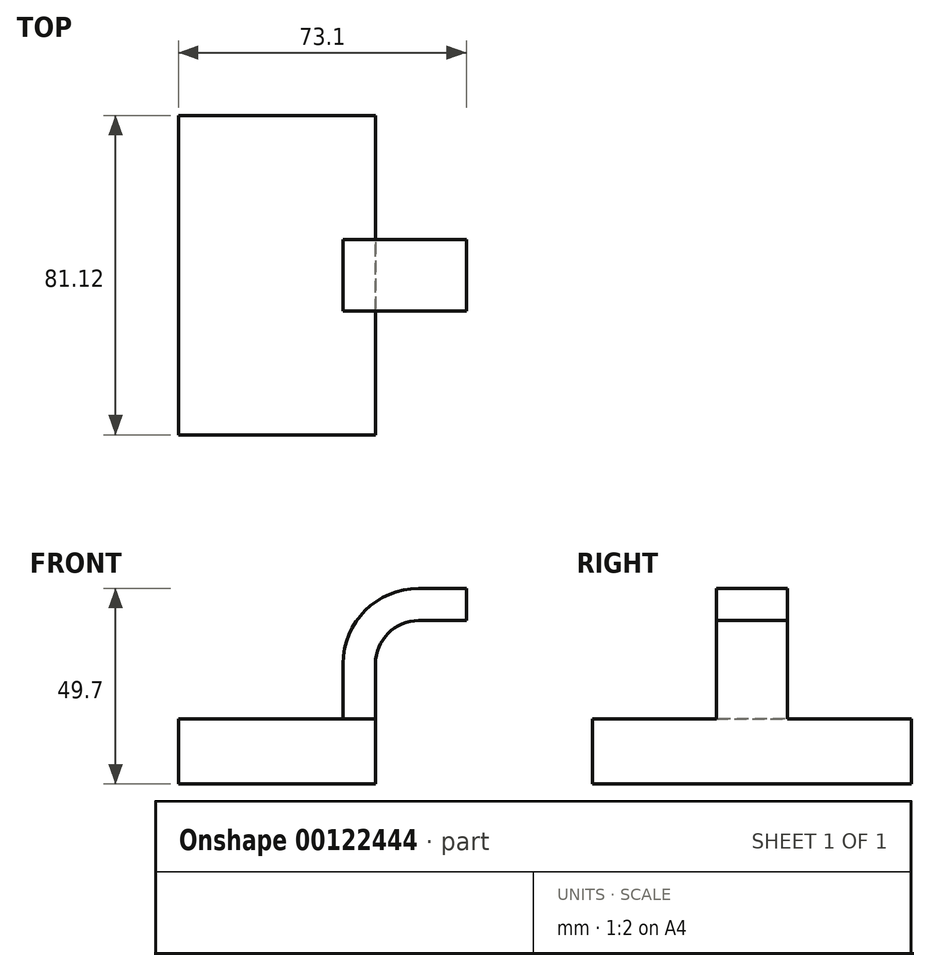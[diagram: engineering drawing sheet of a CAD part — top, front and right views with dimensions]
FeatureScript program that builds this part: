
annotation { "Feature Type Name" : "Feature", "Feature Type Description" : "" }
export const myFeature = defineFeature(function(context is Context, id is Id, definition is map)
    precondition{}
    {
        {
            var Q0;
            Q0=qCreatedBy(makeId("Front.planeOp"),FACE);
            var sketch = newSketch(context, id + "F0", { "sketchPlane" : qUnion([Q0])});
            skLineSegment(sketch, "E0.bottom", {"start": v(-56.67, -13.13) * mm, "end": v(-6.67, -13.13) * mm});
            skLineSegment(sketch, "E0.top", {"start": v(-56.67, -29.63) * mm, "end": v(-6.67, -29.63) * mm});
            skLineSegment(sketch, "E0.left", {"start": v(-56.67, -13.13) * mm, "end": v(-56.67, -29.63) * mm});
            skLineSegment(sketch, "E0.right", {"start": v(-6.67, -13.13) * mm, "end": v(-6.67, -29.63) * mm});
            skLineSegment(sketch, "E1.bottom", {"start": v(4.39, 7.87) * mm, "end": v(25.02, 7.87) * mm});
            skLineSegment(sketch, "E1.top", {"start": v(4.39, 23.87) * mm, "end": v(25.02, 23.87) * mm});
            skLineSegment(sketch, "E1.left", {"start": v(4.39, 7.87) * mm, "end": v(4.39, 23.87) * mm});
            skLineSegment(sketch, "E1.right", {"start": v(25.02, 7.87) * mm, "end": v(25.02, 23.87) * mm});
            skLineSegment(sketch, "E2", {"start": v(-6.67, -13.13) * mm, "end": v(-6.67, 0.87) * mm});
            skArc(sketch, "E3", {"start": v(-6.67, 0.87) * mm, "mid": v(-3.45, 8.65) * mm, "end": v(4.33, 11.87) * mm});
            skLineSegment(sketch, "E4", {"start": v(4.33, 11.87) * mm, "end": v(16.43, 11.87) * mm});
            skLineSegment(sketch, "E5.0", {"start": v(4.33, 20.07) * mm, "end": v(16.43, 20.07) * mm});
            skArc(sketch, "E5.1", {"start": v(-14.87, 0.87) * mm, "mid": v(-9.24, 14.45) * mm, "end": v(4.33, 20.07) * mm});
            skLineSegment(sketch, "E5.2", {"start": v(-14.87, -13.13) * mm, "end": v(-14.87, 0.87) * mm});
            skFitSpline(sketch, "E6", {"points": [v(-56.67, -13.13) * mm, v(4.33, 20.07) * mm], "startDerivative": vector(5.67, 59.32) * mm, "endDerivative": vector(79.25, -1.05) * mm});
            skLineSegment(sketch, "E7", {"start": v(16.43, 11.87) * mm, "end": v(16.43, 20.07) * mm});
            skSolve(sketch);
        }
        {
            var Q0;
            Q0=makeQuery(id+"F0.imprint","IMPRINT",FACE,{"disambiguationData":[TD([[makeQuery(id+"F0.imprint","IMPRINT",EDGE,{"derivedFrom":sQuery(id+"F0.wireOp",EDGE,"E0.top")}),1.0]])]});
            extrude(context, id + "F1", {"entities" : qUnion([Q0]), "endBound" : BoundingType.SYMMETRIC, "oppositeDirection" : true, "depth" : 81.12 * mm});
        }
        {
            var Q0;
            Q0=makeQuery(id+"F0.imprint","IMPRINT",FACE,{"disambiguationData":[TD([[makeQuery(id+"F0.imprint","IMPRINT",EDGE,{"derivedFrom":sQuery(id+"F0.wireOp",EDGE,"E5.1")}),1.0]])]});
            extrude(context, id + "F2", {"entities" : qUnion([Q0]), "operationType" : NewBodyOperationType.ADD, "endBound" : BoundingType.SYMMETRIC, "depth" : 10.78 * mm});
        }
        {
            var Q0;
            {var subQ1=sQuery(id+"F0.wireOp",EDGE,"E2");Q0=makeQuery(id+"F0.imprint","IMPRINT",FACE,{"disambiguationData":[TD([[makeQuery(id+"F0.imprint","IMPRINT",EDGE,{"derivedFrom":subQ1}),1.0]])]});}
            var Q1;
            {var subQ0=sQuery(id+"F0.wireOp",EDGE,"E4");var subQ1=sQuery(id+"F0.wireOp",EDGE,"E1.left");var subQ2=makeQuery(id+"F0.imprint","INTERSECT",VERTEX,{"derivedFrom":[subQ1,subQ0]});Q1=makeQuery(id+"F0.imprint","IMPRINT",FACE,{"disambiguationData":[TD([[makeQuery(id+"F0.imprint","IMPRINT",EDGE,{"disambiguationData":[TD([[subQ2,-1.0]])],"derivedFrom":subQ1}),-1.0]])]});}
            extrude(context, id + "F3", {"entities" : qUnion([Q0, Q1]), "operationType" : NewBodyOperationType.ADD, "endBound" : BoundingType.SYMMETRIC, "depth" : 18.12 * mm});
        }
    });
